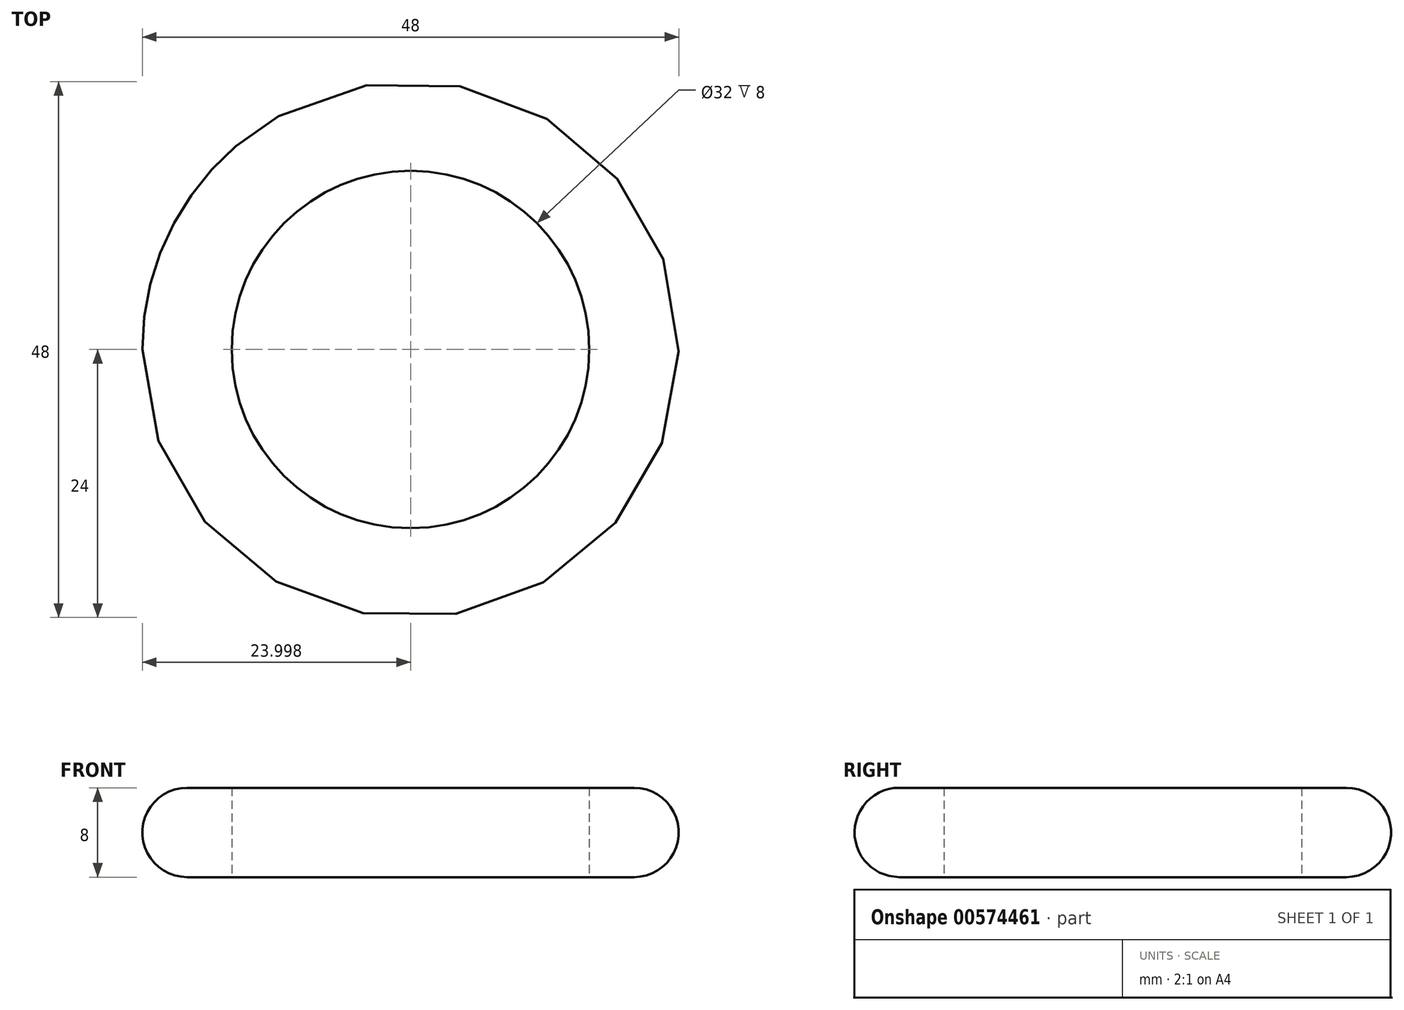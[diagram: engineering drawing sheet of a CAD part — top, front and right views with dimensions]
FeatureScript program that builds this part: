
annotation { "Feature Type Name" : "Feature", "Feature Type Description" : "" }
export const myFeature = defineFeature(function(context is Context, id is Id, definition is map)
    precondition{}
    {
        {
            var Q0;
            Q0=qCreatedBy(makeId("Front.planeOp"),FACE);
            var sketch = newSketch(context, id + "F0", { "sketchPlane" : qUnion([Q0])});
            skLineSegment(sketch, "E0", {"start": v(-8.27, -2.72) * mm, "end": v(-8.27, 8.8) * mm});
            skLineSegment(sketch, "E1", {"start": v(-8.27, -2.72) * mm, "end": v(7.73, -2.72) * mm});
            skLineSegment(sketch, "E2.bottom", {"start": v(7.73, -2.72) * mm, "end": v(11.73, -2.72) * mm});
            skLineSegment(sketch, "E2.top", {"start": v(7.73, 5.28) * mm, "end": v(11.73, 5.28) * mm});
            skLineSegment(sketch, "E2.left", {"start": v(7.73, -2.72) * mm, "end": v(7.73, 5.28) * mm});
            skLineSegment(sketch, "E2.right", {"start": v(11.73, -2.72) * mm, "end": v(11.73, 5.28) * mm});
            skArc(sketch, "E3", {"start": v(11.73, -2.72) * mm, "mid": v(15.73, 1.28) * mm, "end": v(11.73, 5.28) * mm});
            skSolve(sketch);
        }
        {
            var Q0;
            Q0=qSketchRegion(id+"F0",true);
            var Q1;
            Q1=sQuery(id+"F0.wireOp",EDGE,"E0");
            revolve(context, id + "F1", {"surfaceOperationType" : NewSurfaceOperationType.NEW, "entities" : qUnion([Q0]), "axis" : qUnion([Q1]), "revolveType" : RevolveType.FULL});
        }
    });
